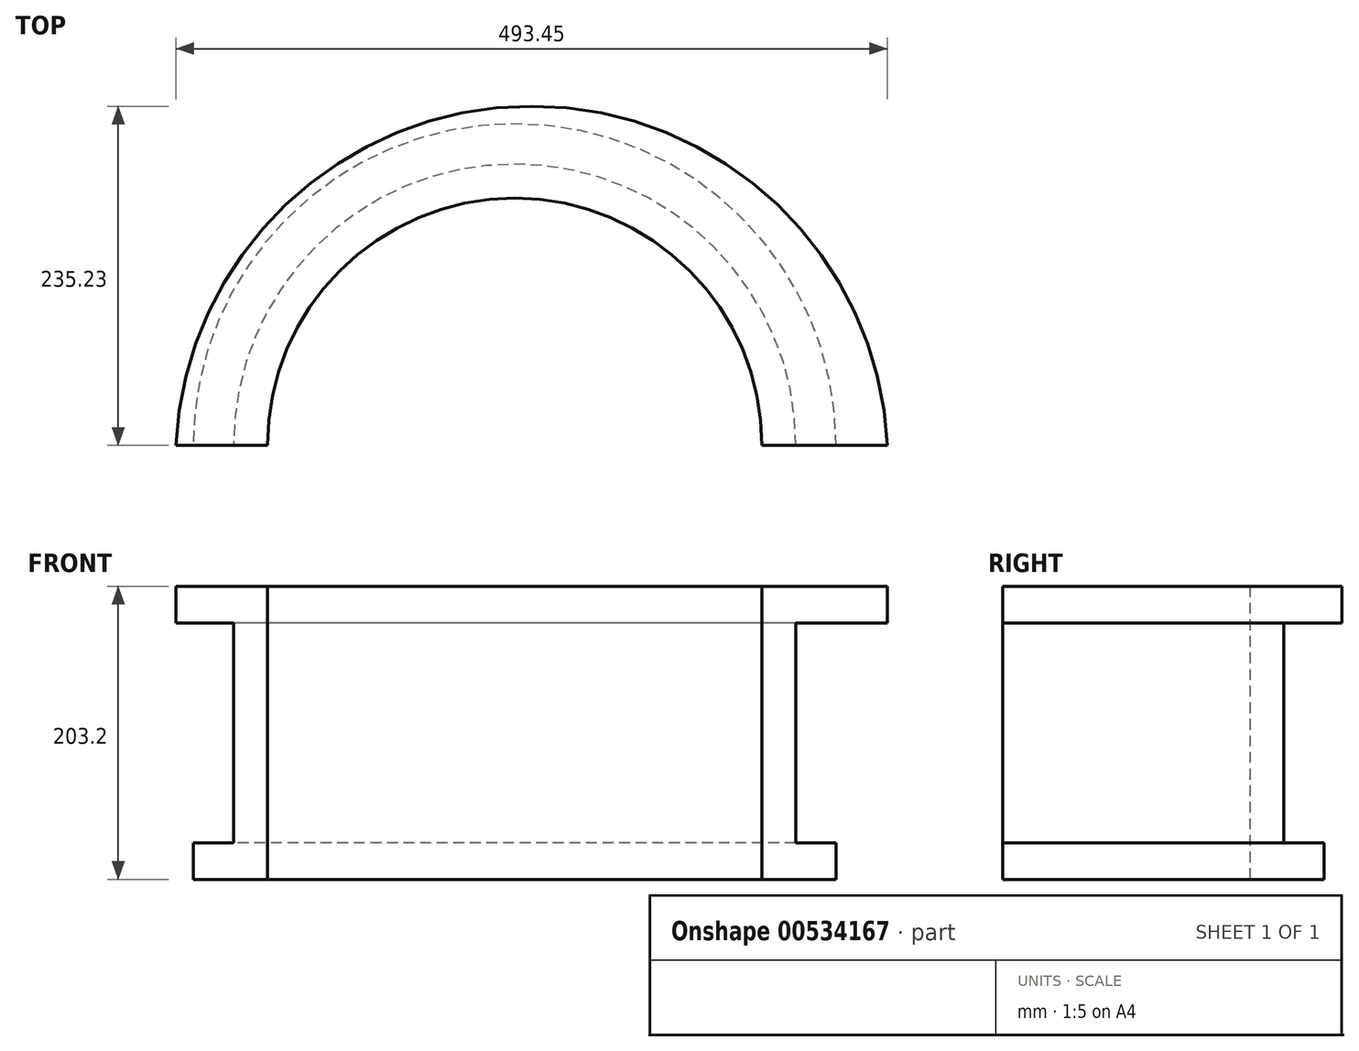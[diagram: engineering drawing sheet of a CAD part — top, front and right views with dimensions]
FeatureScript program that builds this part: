
annotation { "Feature Type Name" : "Feature", "Feature Type Description" : "" }
export const myFeature = defineFeature(function(context is Context, id is Id, definition is map)
    precondition{}
    {
        {
            var Q0;
            Q0=qCreatedBy(makeId("Top.planeOp"),FACE);
            var sketch = newSketch(context, id + "F0", { "sketchPlane" : qUnion([Q0])});
            skCircle(sketch, "E0", {"center": v(0, 0) * mm, "radius": 195 * mm});
            skLineSegment(sketch, "E1", {"start": v(0, 0) * mm, "end": v(-195, 0) * mm});
            skLineSegment(sketch, "E2", {"start": v(0, 0) * mm, "end": v(195, 0) * mm});
            skCircle(sketch, "E3", {"center": v(0, 0) * mm, "radius": 171.45 * mm});
            skSolve(sketch);
        }
        {
            var Q0;
            {var subQ0=sQuery(id+"F0.wireOp",EDGE,"E1");var subQ1=sQuery(id+"F0.wireOp",EDGE,"E0");var subQ2=makeQuery(id+"F0.imprint","INTERSECT",VERTEX,{"derivedFrom":[subQ1,subQ0]});Q0=makeQuery(id+"F0.imprint","IMPRINT",FACE,{"disambiguationData":[TD([[makeQuery(id+"F0.imprint","IMPRINT",EDGE,{"disambiguationData":[TD([[subQ2,1.0]])],"derivedFrom":subQ1}),1.0]])]});}
            extrude(context, id + "F1", {"entities" : qUnion([Q0]), "depth" : 152.4 * mm, "offsetDistance" : 25.4 * mm});
        }
        {
            var Q0;
            Q0=makeQuery(id+"F1.opExtrude","CAP_FACE",FACE,{"disambiguationData":[OSD([sQuery(id+"F0.wireOp",EDGE,"E0"),sQuery(id+"F0.wireOp",EDGE,"E1"),sQuery(id+"F0.wireOp",EDGE,"E2"),sQuery(id+"F0.wireOp",EDGE,"E3")])],"isStart":true});
            var sketch = newSketch(context, id + "F2", { "sketchPlane" : qUnion([Q0])});
            skLineSegment(sketch, "E4", {"start": v(-171.45, 0) * mm, "end": v(-222.25, 0) * mm});
            skLineSegment(sketch, "E5.MirrorCS", {"start": v(171.45, 0) * mm, "end": v(222.25, 0) * mm});
            skArc(sketch, "E6", {"start": v(-222.95, 0) * mm, "mid": v(0, -222.95) * mm, "end": v(222.95, 0) * mm});
            skLineSegment(sketch, "E7", {"start": v(-171.45, 0) * mm, "end": v(-222.95, 0) * mm});
            skLineSegment(sketch, "E8", {"start": v(-222.95, 0) * mm, "end": v(-171.45, 0) * mm});
            skLineSegment(sketch, "E9.trimOffspring", {"start": v(222.25, 0) * mm, "end": v(222.95, 0) * mm});
            skSolve(sketch);
        }
        {
            var Q0;
            {var subQ2=sQuery(id+"F2.wireOp",EDGE,"E6");Q0=makeQuery(id+"F2.imprint","IMPRINT",FACE,{"disambiguationData":[TD([[makeQuery(id+"F2.imprint","IMPRINT",EDGE,{"derivedFrom":subQ2}),1.0]])]});}
            var Q1;
            {var subQ1=makeQuery(id+"F1.opExtrude","CAP_EDGE",EDGE,{"disambiguationData":[OSD([sQuery(id+"F0.wireOp",EDGE,"E0")])],"isStart":true});Q1=makeQuery(id+"F2.imprint","IMPRINT",FACE,{"disambiguationData":[TD([[makeQuery(id+"F2.imprint","IMPRINT",EDGE,{"derivedFrom":subQ1}),-1.0]])]});}
            var Q2;
            Q2=makeQuery(id+"F1.opExtrude","CAP_FACE",FACE,{"disambiguationData":[OSD([sQuery(id+"F0.wireOp",EDGE,"E0"),sQuery(id+"F0.wireOp",EDGE,"E1"),sQuery(id+"F0.wireOp",EDGE,"E2"),sQuery(id+"F0.wireOp",EDGE,"E3")])],"isStart":false});
            extrude(context, id + "F3", {"entities" : qUnion([Q0, Q1, Q2]), "operationType" : NewBodyOperationType.ADD, "depth" : 25.4 * mm, "offsetDistance" : 25.4 * mm});
        }
        {
            var Q0;
            Q0=makeQuery(id+"F1.opExtrude","CAP_FACE",FACE,{"disambiguationData":[OSD([sQuery(id+"F0.wireOp",EDGE,"E0"),sQuery(id+"F0.wireOp",EDGE,"E1"),sQuery(id+"F0.wireOp",EDGE,"E2"),sQuery(id+"F0.wireOp",EDGE,"E3")])],"isStart":false});
            var sketch = newSketch(context, id + "F4", { "sketchPlane" : qUnion([Q0])});
            skPoint(sketch, "E10.endSnap0", {"position": v(-183.23, 0) * mm});
            skLineSegment(sketch, "E11", {"start": v(195, 0) * mm, "end": v(258.5, 0) * mm});
            skLineSegment(sketch, "E12", {"start": v(-171.45, 0) * mm, "end": v(-234.95, 0) * mm});
            skLineSegment(sketch, "E13", {"start": v(0, 171.45) * mm, "end": v(0, 234.95) * mm});
            skPoint(sketch, "E13.endSnap0", {"position": v(0, 195) * mm});
            skArc(sketch, "E14", {"start": v(258.5, 0) * mm, "mid": v(11.77, 235.23) * mm, "end": v(-234.95, 0) * mm});
            skSolve(sketch);
        }
        {
            var Q0;
            {var subQ0=sQuery(id+"F4.wireOp",EDGE,"E12");var subQ1=makeQuery(id+"F1.opExtrude","CAP_EDGE",EDGE,{"disambiguationData":[OSD([sQuery(id+"F0.wireOp",EDGE,"E0")])],"isStart":false});var subQ2=makeQuery(id+"F4.imprint","INTERSECT",VERTEX,{"derivedFrom":[subQ1,subQ0]});Q0=makeQuery(id+"F4.imprint","IMPRINT",FACE,{"disambiguationData":[TD([[makeQuery(id+"F4.imprint","IMPRINT",EDGE,{"disambiguationData":[TD([[subQ2,-1.0]])],"derivedFrom":subQ0}),-1.0]])]});}
            var Q1;
            {var subQ0=sQuery(id+"F4.wireOp",EDGE,"E12");var subQ1=makeQuery(id+"F1.opExtrude","CAP_EDGE",EDGE,{"disambiguationData":[OSD([sQuery(id+"F0.wireOp",EDGE,"E0")])],"isStart":false});var subQ2=makeQuery(id+"F4.imprint","INTERSECT",VERTEX,{"derivedFrom":[subQ1,subQ0]});Q1=makeQuery(id+"F4.imprint","IMPRINT",FACE,{"disambiguationData":[TD([[makeQuery(id+"F4.imprint","IMPRINT",EDGE,{"disambiguationData":[TD([[subQ2,1.0]])],"derivedFrom":subQ0}),-1.0]])]});}
            var Q2;
            {var subQ0=sQuery(id+"F4.wireOp",EDGE,"E11");Q2=makeQuery(id+"F4.imprint","IMPRINT",FACE,{"disambiguationData":[TD([[makeQuery(id+"F4.imprint","IMPRINT",EDGE,{"derivedFrom":subQ0}),1.0]])]});}
            var Q3;
            {var subQ5=makeQuery(id+"F1.opExtrude","CAP_EDGE",EDGE,{"disambiguationData":[OSD([sQuery(id+"F0.wireOp",EDGE,"E2")])],"isStart":false});Q3=makeQuery(id+"F4.imprint","IMPRINT",FACE,{"disambiguationData":[TD([[makeQuery(id+"F4.imprint","IMPRINT",EDGE,{"derivedFrom":subQ5}),1.0]])]});}
            extrude(context, id + "F5", {"entities" : qUnion([Q0, Q1, Q2, Q3]), "operationType" : NewBodyOperationType.ADD, "depth" : 25.4 * mm, "offsetDistance" : 25.4 * mm});
        }
    });
